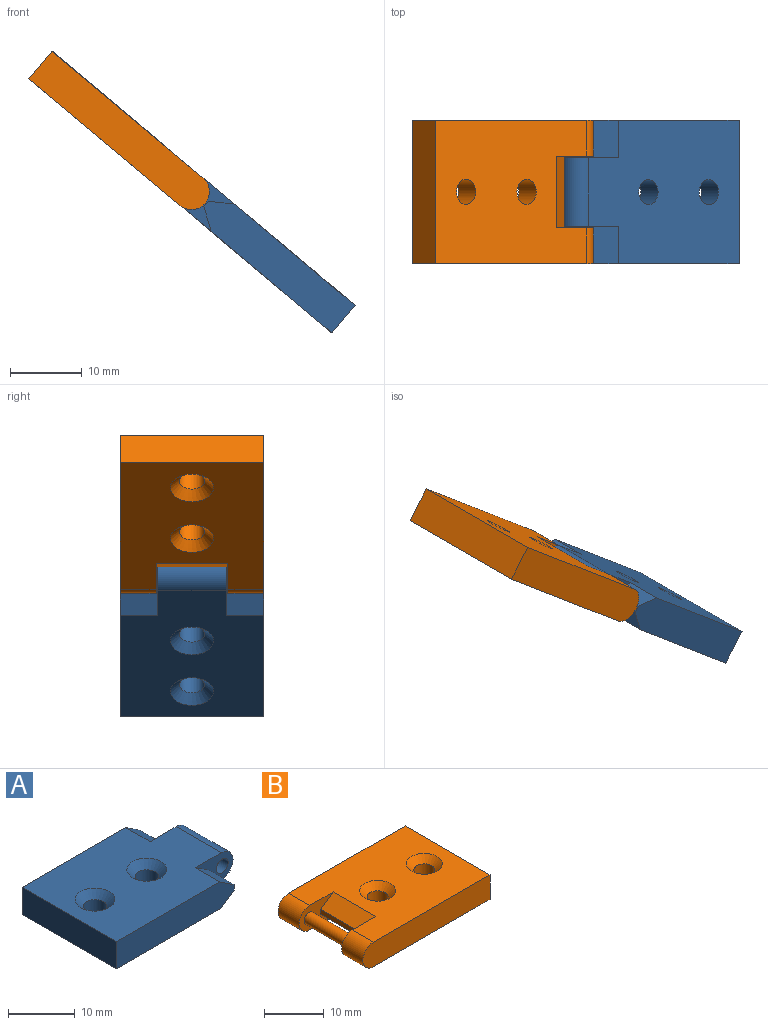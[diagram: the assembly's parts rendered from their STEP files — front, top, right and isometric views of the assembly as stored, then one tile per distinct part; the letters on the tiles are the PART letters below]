
ASSEMBLY  parts=2 mates=1
PART A: 19 faces, bbox 30x20x5 mm
  f0: cylinder r=2.5mm len=9.6mm, axis (0,1,0), area 75.4mm2, adj f2,f3,f7,f9
  f1: plane 25x5mm, normal (0,1,0), area 119mm2, adj f2,f3,f4,f6,f13,f14
  f2: plane 27.5x20mm, normal (0,0,1), area 436.3mm2, adj f0,f1,f4,f5,f7,f9,f11,f13
  f3: plane 27.5x20mm, normal (0,0,-1), area 473.6mm2, adj f0,f1,f4,f5,f7,f9,f12,f14
  f4: plane 20x5mm, normal (-1,0,0), area 100mm2, adj f1,f2,f3,f5
  f5: plane 25x5mm, normal (0,-1,0), area 119mm2, adj f2,f3,f4,f8,f11,f12
  f6: plane 5.2x1mm, normal (1,0,0), area 5.2mm2, adj f1,f7,f13,f14
  f7: plane 8x5mm, normal (0,1,0), area 23.4mm2, adj f0,f2,f3,f6,f10,f13,f14
  f8: plane 5.2x1mm, normal (1,0,0), area 5.2mm2, adj f5,f9,f11,f12
  f9: plane 8x5mm, normal (0,-1,0), area 23.4mm2, adj f0,f2,f3,f8,f10,f11,f12
  f10: cylinder r=1.25mm len=9.6mm, axis (0,1,0), area 75.4mm2, adj f7,f9
  f11: plane 5.2x3mm, normal (0.55,0,0.83), area 18.7mm2, adj f2,f5,f8,f9
  f12: plane 5.2x3mm, normal (0.55,0,-0.83), area 18.7mm2, adj f3,f5,f8,f9
  f13: plane 5.2x3mm, normal (0.55,0,0.83), area 18.7mm2, adj f1,f2,f6,f7
  f14: plane 5.2x3mm, normal (0.55,0,-0.83), area 18.7mm2, adj f1,f3,f6,f7
  f15: cylinder r=1.75mm len=3.75mm, axis (0,0,1), area 41.2mm2, adj f3,f16
  f16: cone r=1.75mm half-angle=45deg, axis (0,0,1), area 26.4mm2, adj f2,f15
  f17: cylinder r=1.75mm len=3.75mm, axis (0,0,1), area 41.2mm2, adj f3,f18
  f18: cone r=1.75mm half-angle=45deg, axis (0,0,1), area 26.4mm2, adj f2,f17
PART B: 17 faces, bbox 30x20x5 mm
  f0: plane 10x1mm, normal (-1,0,0), area 10mm2, adj f7,f9,f11,f12
  f1: plane 20x5mm, normal (1,0,0), area 100mm2, adj f2,f3,f4,f5
  f2: plane 30x5mm, normal (0,1,0), area 147.3mm2, adj f1,f4,f5,f6
  f3: plane 30x5mm, normal (0,-1,0), area 147.3mm2, adj f1,f4,f5,f8
  f4: plane 27.5x20mm, normal (0,0,1), area 438.5mm2, adj f1,f2,f3,f6,f7,f8,f9,f11
  f5: plane 27.5x20mm, normal (0,0,-1), area 475.8mm2, adj f1,f2,f3,f6,f7,f8,f9,f12
  f6: cylinder r=2.5mm len=5mm, axis (0,1,0), area 39.3mm2, adj f2,f4,f5,f7
  f7: plane 8x5mm, normal (0,-1,0), area 24.2mm2, adj f0,f4,f5,f6,f10,f11,f12
  f8: cylinder r=2.5mm len=5mm, axis (0,-1,0), area 39.3mm2, adj f3,f4,f5,f9
  f9: plane 8x5mm, normal (0,1,0), area 24.2mm2, adj f0,f4,f5,f8,f10,f11,f12
  f10: cylinder r=1.15mm len=10mm, axis (0,-1,0), area 72.3mm2, adj f7,f9
  f11: plane 10x3mm, normal (-0.55,0,0.83), area 36.1mm2, adj f0,f4,f7,f9
  f12: plane 10x3mm, normal (-0.55,0,-0.83), area 36.1mm2, adj f0,f5,f7,f9
  f13: cylinder r=1.75mm len=3.75mm, axis (0,0,1), area 41.2mm2, adj f5,f14
  f14: cone r=1.75mm half-angle=45deg, axis (0,0,1), area 26.4mm2, adj f4,f13
  f15: cylinder r=1.75mm len=3.75mm, axis (0,0,1), area 41.2mm2, adj f5,f16
  f16: cone r=1.75mm half-angle=45deg, axis (0,0,1), area 26.4mm2, adj f4,f15
PLACE A rot(axis=(0,-1,0),140deg) t=(33.08,6.06,-2.03)mm
PLACE B rot(axis=(0,-1,0),140deg) t=(9.95,6.06,17.38)mm
MATE revolute B.f10 <-> A.f0  axis (0,-1,0) through (21.59,6.06,7.61)mm
